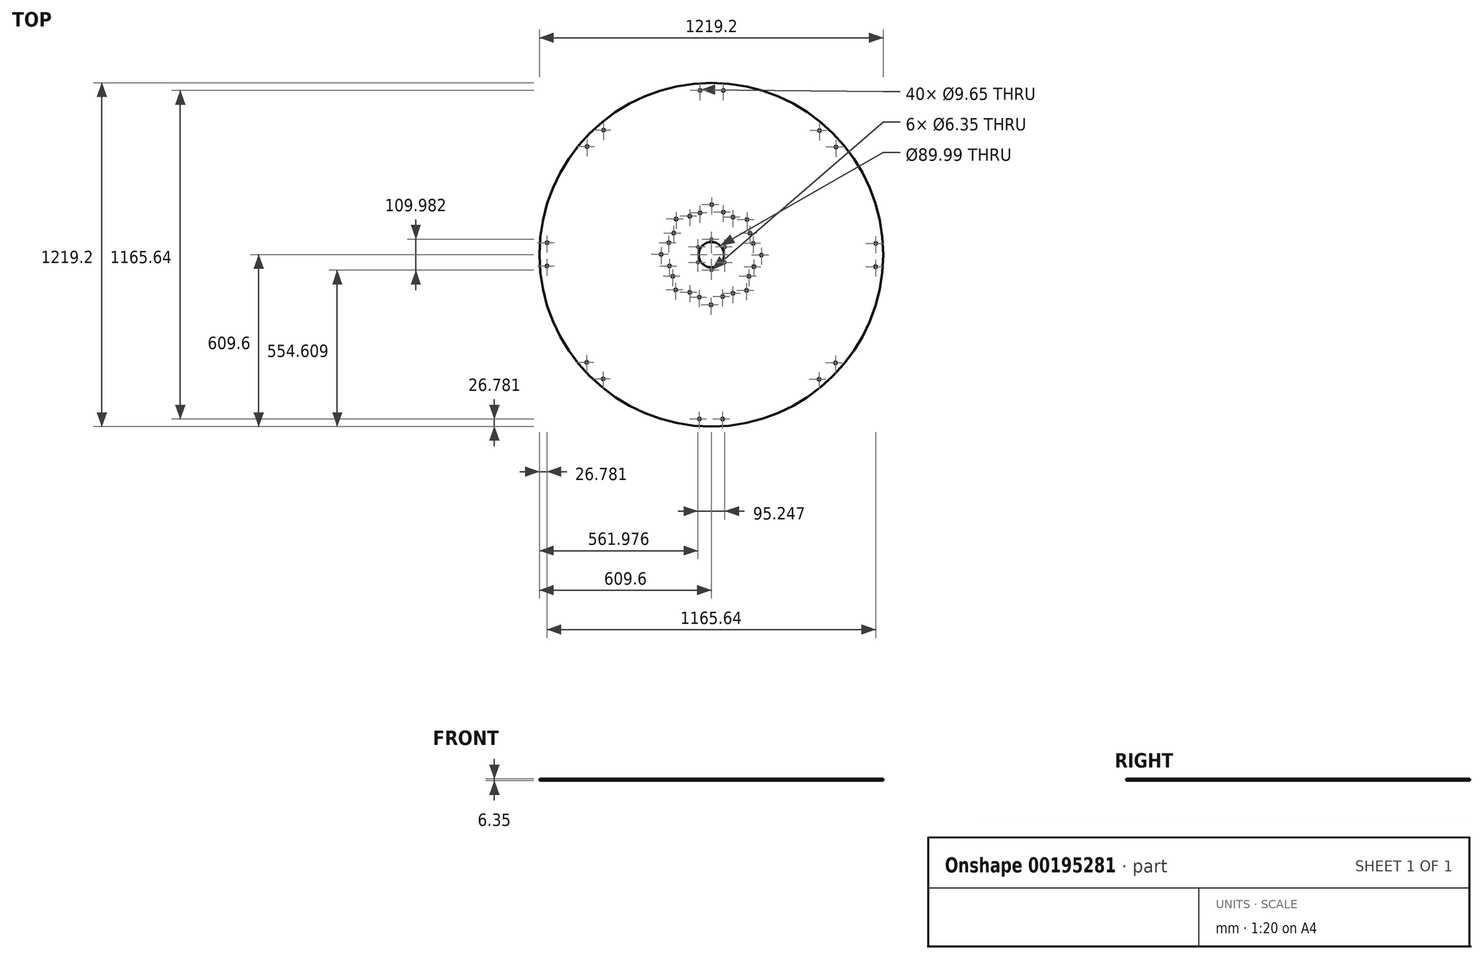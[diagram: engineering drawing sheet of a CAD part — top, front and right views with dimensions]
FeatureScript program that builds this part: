
annotation { "Feature Type Name" : "Feature", "Feature Type Description" : "" }
export const myFeature = defineFeature(function(context is Context, id is Id, definition is map)
    precondition{}
    {
        {
            var Q0;
            Q0=qCreatedBy(makeId("Top.planeOp"),FACE);
            var sketch = newSketch(context, id + "F0", { "sketchPlane" : qUnion([Q0])});
            skCircle(sketch, "E0", {"center": v(0, 0) * mm, "radius": 45 * mm});
            skCircle(sketch, "E1", {"center": v(0, 0) * mm, "radius": 65 * mm, "construction": true});
            skCircle(sketch, "E2", {"center": v(0, 55) * mm, "radius": 3.18 * mm});
            skCircle(sketch, "E3.1.0", {"center": v(-47.62, 27.5) * mm, "radius": 3.18 * mm});
            skCircle(sketch, "E3.2.0", {"center": v(-47.62, -27.5) * mm, "radius": 3.18 * mm});
            skCircle(sketch, "E3.3.0", {"center": v(0, -55) * mm, "radius": 3.18 * mm});
            skCircle(sketch, "E3.4.0", {"center": v(47.62, -27.5) * mm, "radius": 3.18 * mm});
            skCircle(sketch, "E3.5.0", {"center": v(47.62, 27.5) * mm, "radius": 3.18 * mm});
            skCircle(sketch, "E4", {"center": v(0, 0) * mm, "radius": 609.6 * mm});
            skPoint(sketch, "E5.center", {"position": v(0.6, 0) * mm});
            skCircle(sketch, "E6", {"center": v(-40.14, 582.82) * mm, "radius": 4.83 * mm});
            skCircle(sketch, "E7", {"center": v(42.4, 582.66) * mm, "radius": 4.83 * mm});
            skCircle(sketch, "E8.1.0", {"center": v(-440.5, 383.73) * mm, "radius": 4.83 * mm});
            skCircle(sketch, "E8.1.1", {"center": v(-382.02, 441.99) * mm, "radius": 4.83 * mm});
            skCircle(sketch, "E8.2.0", {"center": v(-582.82, -40.14) * mm, "radius": 4.83 * mm});
            skCircle(sketch, "E8.2.1", {"center": v(-582.66, 42.4) * mm, "radius": 4.83 * mm});
            skCircle(sketch, "E8.3.0", {"center": v(-383.73, -440.5) * mm, "radius": 4.83 * mm});
            skCircle(sketch, "E8.3.1", {"center": v(-441.99, -382.02) * mm, "radius": 4.83 * mm});
            skCircle(sketch, "E8.4.0", {"center": v(40.14, -582.82) * mm, "radius": 4.83 * mm});
            skCircle(sketch, "E8.4.1", {"center": v(-42.4, -582.66) * mm, "radius": 4.83 * mm});
            skCircle(sketch, "E8.5.0", {"center": v(440.5, -383.73) * mm, "radius": 4.83 * mm});
            skCircle(sketch, "E8.5.1", {"center": v(382.02, -441.99) * mm, "radius": 4.83 * mm});
            skCircle(sketch, "E8.6.0", {"center": v(582.82, 40.14) * mm, "radius": 4.83 * mm});
            skCircle(sketch, "E8.6.1", {"center": v(582.66, -42.4) * mm, "radius": 4.83 * mm});
            skCircle(sketch, "E8.7.0", {"center": v(383.73, 440.5) * mm, "radius": 4.83 * mm});
            skCircle(sketch, "E8.7.1", {"center": v(441.99, 382.02) * mm, "radius": 4.83 * mm});
            skCircle(sketch, "E9", {"center": v(42.55, 150.86) * mm, "radius": 4.83 * mm});
            skCircle(sketch, "E10", {"center": v(-40.16, 148.45) * mm, "radius": 4.83 * mm});
            skCircle(sketch, "E11", {"center": v(1.2, 177.8) * mm, "radius": 4.83 * mm});
            skCircle(sketch, "E12.1.0", {"center": v(-133.36, 76.57) * mm, "radius": 4.83 * mm});
            skCircle(sketch, "E12.1.1", {"center": v(-124.88, 126.57) * mm, "radius": 4.83 * mm});
            skCircle(sketch, "E12.1.2", {"center": v(-76.59, 136.76) * mm, "radius": 4.83 * mm});
            skCircle(sketch, "E12.2.0", {"center": v(-148.45, -40.16) * mm, "radius": 4.83 * mm});
            skCircle(sketch, "E12.2.1", {"center": v(-177.8, 1.2) * mm, "radius": 4.83 * mm});
            skCircle(sketch, "E12.2.2", {"center": v(-150.86, 42.55) * mm, "radius": 4.83 * mm});
            skCircle(sketch, "E12.3.0", {"center": v(-76.57, -133.36) * mm, "radius": 4.83 * mm});
            skCircle(sketch, "E12.3.1", {"center": v(-126.57, -124.88) * mm, "radius": 4.83 * mm});
            skCircle(sketch, "E12.3.2", {"center": v(-136.76, -76.59) * mm, "radius": 4.83 * mm});
            skCircle(sketch, "E12.4.0", {"center": v(40.16, -148.45) * mm, "radius": 4.83 * mm});
            skCircle(sketch, "E12.4.1", {"center": v(-1.2, -177.8) * mm, "radius": 4.83 * mm});
            skCircle(sketch, "E12.4.2", {"center": v(-42.55, -150.86) * mm, "radius": 4.83 * mm});
            skCircle(sketch, "E12.5.0", {"center": v(133.36, -76.57) * mm, "radius": 4.83 * mm});
            skCircle(sketch, "E12.5.1", {"center": v(124.88, -126.57) * mm, "radius": 4.83 * mm});
            skCircle(sketch, "E12.5.2", {"center": v(76.59, -136.76) * mm, "radius": 4.83 * mm});
            skCircle(sketch, "E12.6.0", {"center": v(148.45, 40.16) * mm, "radius": 4.83 * mm});
            skCircle(sketch, "E12.6.1", {"center": v(177.8, -1.2) * mm, "radius": 4.83 * mm});
            skCircle(sketch, "E12.6.2", {"center": v(150.86, -42.55) * mm, "radius": 4.83 * mm});
            skCircle(sketch, "E12.7.0", {"center": v(76.57, 133.36) * mm, "radius": 4.83 * mm});
            skCircle(sketch, "E12.7.1", {"center": v(126.57, 124.88) * mm, "radius": 4.83 * mm});
            skCircle(sketch, "E12.7.2", {"center": v(136.76, 76.59) * mm, "radius": 4.83 * mm});
            skLineSegment(sketch, "E13", {"start": v(-382.02, 441.99) * mm, "end": v(-76.59, 136.76) * mm, "construction": true});
            skLineSegment(sketch, "E14", {"start": v(-440.5, 383.73) * mm, "end": v(-133.36, 76.57) * mm, "construction": true});
            skLineSegment(sketch, "E15.1.0", {"start": v(-581.69, 41.43) * mm, "end": v(-149.89, 41.57) * mm, "construction": true});
            skLineSegment(sketch, "E15.1.1", {"start": v(-581.85, -41.12) * mm, "end": v(-147.47, -41.13) * mm, "construction": true});
            skLineSegment(sketch, "E15.2.0", {"start": v(-439.64, -382.99) * mm, "end": v(-134.4, -77.56) * mm, "construction": true});
            skLineSegment(sketch, "E15.2.1", {"start": v(-381.38, -441.47) * mm, "end": v(-74.22, -134.34) * mm, "construction": true});
            skLineSegment(sketch, "E15.3.0", {"start": v(-39.08, -582.66) * mm, "end": v(-39.22, -150.86) * mm, "construction": true});
            skLineSegment(sketch, "E15.3.1", {"start": v(43.47, -582.82) * mm, "end": v(43.48, -148.45) * mm, "construction": true});
            skLineSegment(sketch, "E15.4.0", {"start": v(385.34, -440.61) * mm, "end": v(79.91, -135.38) * mm, "construction": true});
            skLineSegment(sketch, "E15.4.1", {"start": v(443.82, -382.35) * mm, "end": v(136.69, -75.2) * mm, "construction": true});
            skLineSegment(sketch, "E15.5.0", {"start": v(585, -40.06) * mm, "end": v(153.2, -40.2) * mm, "construction": true});
            skLineSegment(sketch, "E15.5.1", {"start": v(585.17, 42.5) * mm, "end": v(150.8, 42.5) * mm, "construction": true});
            skLineSegment(sketch, "E15.6.0", {"start": v(442.96, 384.37) * mm, "end": v(137.73, 78.94) * mm, "construction": true});
            skLineSegment(sketch, "E15.6.1", {"start": v(384.7, 442.85) * mm, "end": v(77.55, 135.71) * mm, "construction": true});
            skLineSegment(sketch, "E15.7.0", {"start": v(42.4, 584.04) * mm, "end": v(42.55, 152.24) * mm, "construction": true});
            skLineSegment(sketch, "E15.7.1", {"start": v(-40.14, 584.2) * mm, "end": v(-40.16, 149.82) * mm, "construction": true});
            skPoint(sketch, "E15.center", {"position": v(1.66, 0.69) * mm});
            skSolve(sketch);
        }
        {
            var Q0;
            Q0=makeQuery(id+"F0.imprint","IMPRINT",FACE,{"disambiguationData":[TD([[makeQuery(id+"F0.imprint","IMPRINT",EDGE,{"derivedFrom":sQuery(id+"F0.wireOp",EDGE,"E0")}),-1.0]])]});
            extrude(context, id + "F1", {"entities" : qUnion([Q0]), "depth" : 6.35 * mm});
        }
    });
